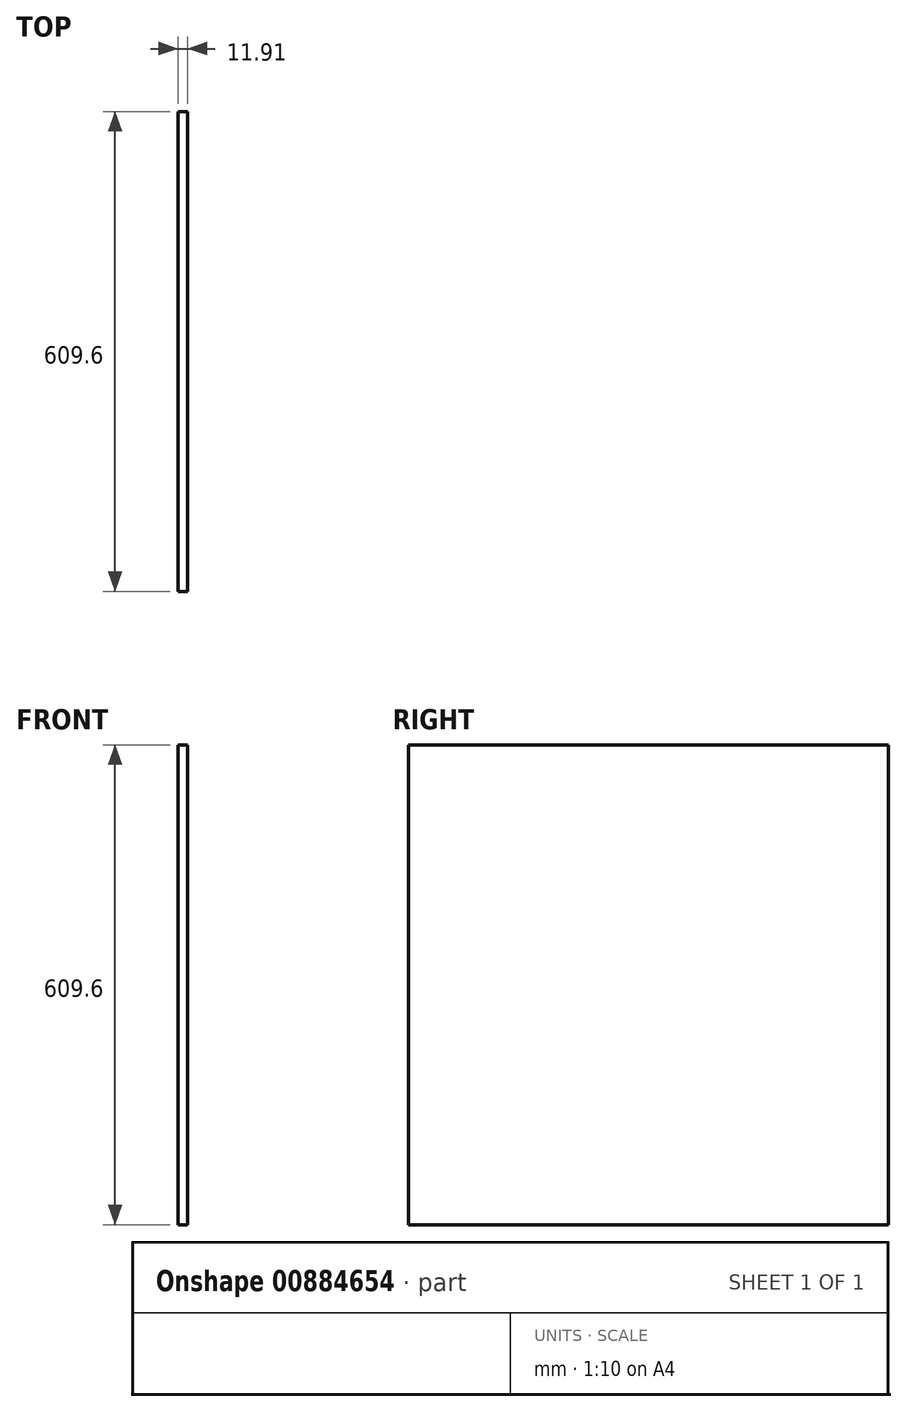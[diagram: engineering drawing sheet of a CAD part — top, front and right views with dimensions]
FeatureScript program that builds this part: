
annotation { "Feature Type Name" : "Feature", "Feature Type Description" : "" }
export const myFeature = defineFeature(function(context is Context, id is Id, definition is map)
    precondition{}
    {
        {
            var Q0;
            Q0=qCreatedBy(makeId("Right.planeOp"),FACE);
            var sketch = newSketch(context, id + "F0", { "sketchPlane" : qUnion([Q0])});
            skLineSegment(sketch, "E0.bottom", {"start": v(-304.8, 238.31) * mm, "end": v(304.8, 238.31) * mm});
            skLineSegment(sketch, "E0.top", {"start": v(-304.8, -371.29) * mm, "end": v(304.8, -371.29) * mm});
            skLineSegment(sketch, "E0.left", {"start": v(-304.8, 238.31) * mm, "end": v(-304.8, -371.29) * mm});
            skLineSegment(sketch, "E0.right", {"start": v(304.8, 238.31) * mm, "end": v(304.8, -371.29) * mm});
            skSolve(sketch);
        }
        {
            var Q0;
            Q0 = qSketchRegion(id + "F0", true);
            extrude(context, id + "F1", {"entities" : qUnion([Q0]), "depth" : 11.9 * mm, "offsetDistance" : 25.4 * mm});
        }
    });
